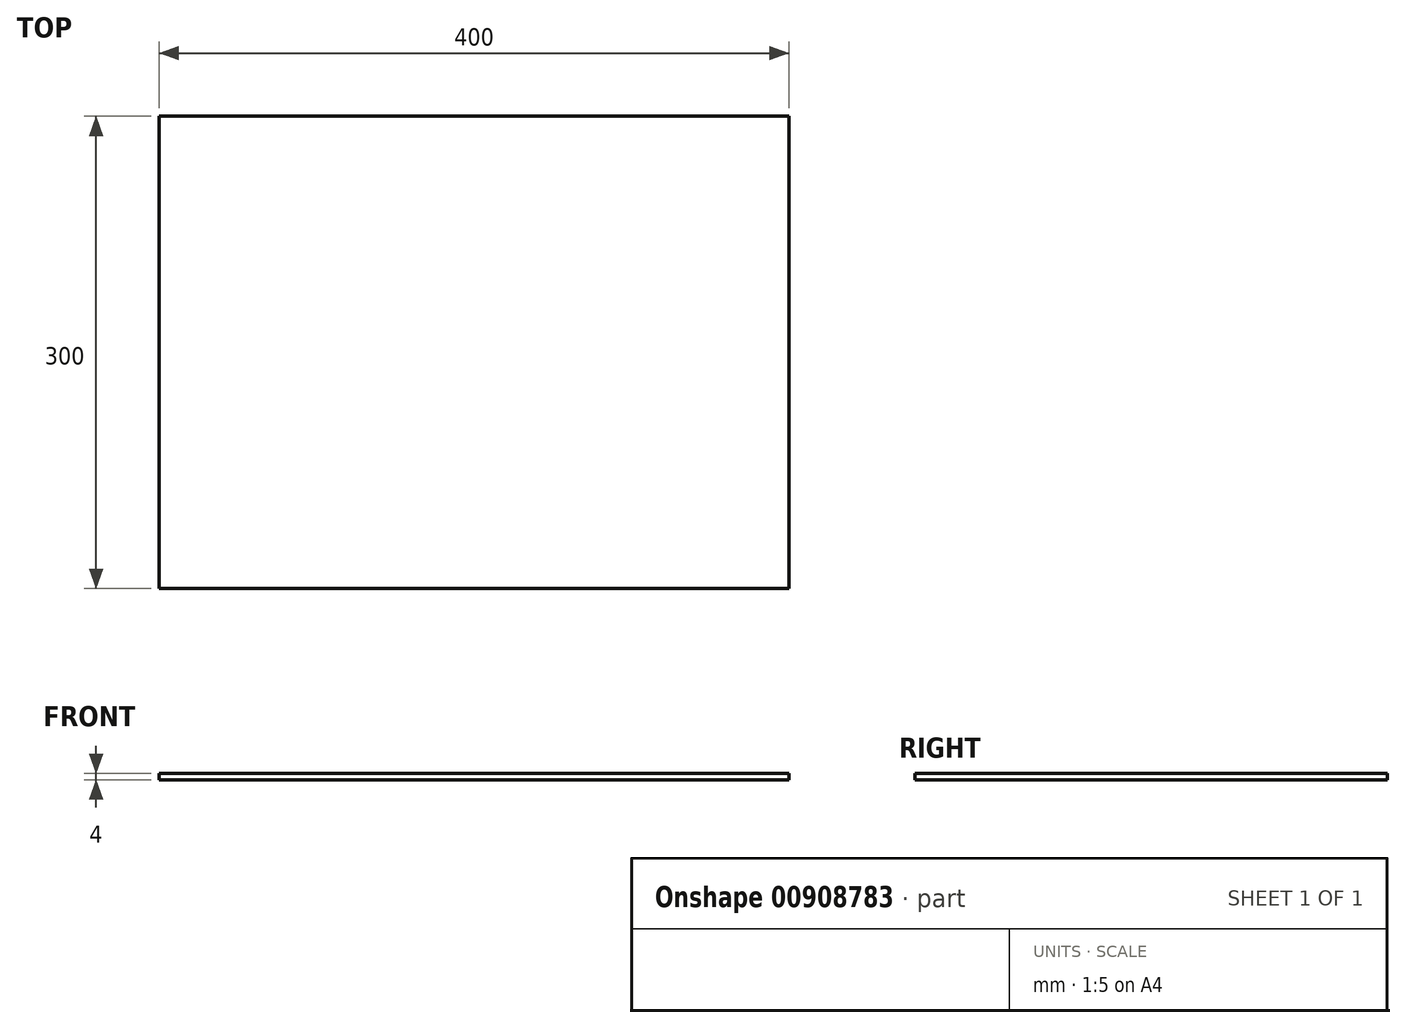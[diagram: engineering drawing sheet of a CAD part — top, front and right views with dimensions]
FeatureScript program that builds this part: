
annotation { "Feature Type Name" : "Feature", "Feature Type Description" : "" }
export const myFeature = defineFeature(function(context is Context, id is Id, definition is map)
    precondition{}
    {
        {
            var Q0;
            Q0=qCreatedBy(makeId("Top.planeOp"),FACE);
            var sketch = newSketch(context, id + "F0", { "sketchPlane" : qUnion([Q0])});
            skLineSegment(sketch, "E0.bottom", {"start": v(-200, 150) * mm, "end": v(200, 150) * mm});
            skLineSegment(sketch, "E0.top", {"start": v(-200, -150) * mm, "end": v(200, -150) * mm});
            skLineSegment(sketch, "E0.left", {"start": v(-200, 150) * mm, "end": v(-200, -150) * mm});
            skLineSegment(sketch, "E0.right", {"start": v(200, 150) * mm, "end": v(200, -150) * mm});
            skSolve(sketch);
        }
        {
            var Q0;
            Q0=qSketchRegion(id+"F0",true);
            extrude(context, id + "F1", {"entities" : qUnion([Q0]), "oppositeDirection" : true, "depth" : 4 * mm, "offsetDistance" : 25 * mm});
        }
    });
